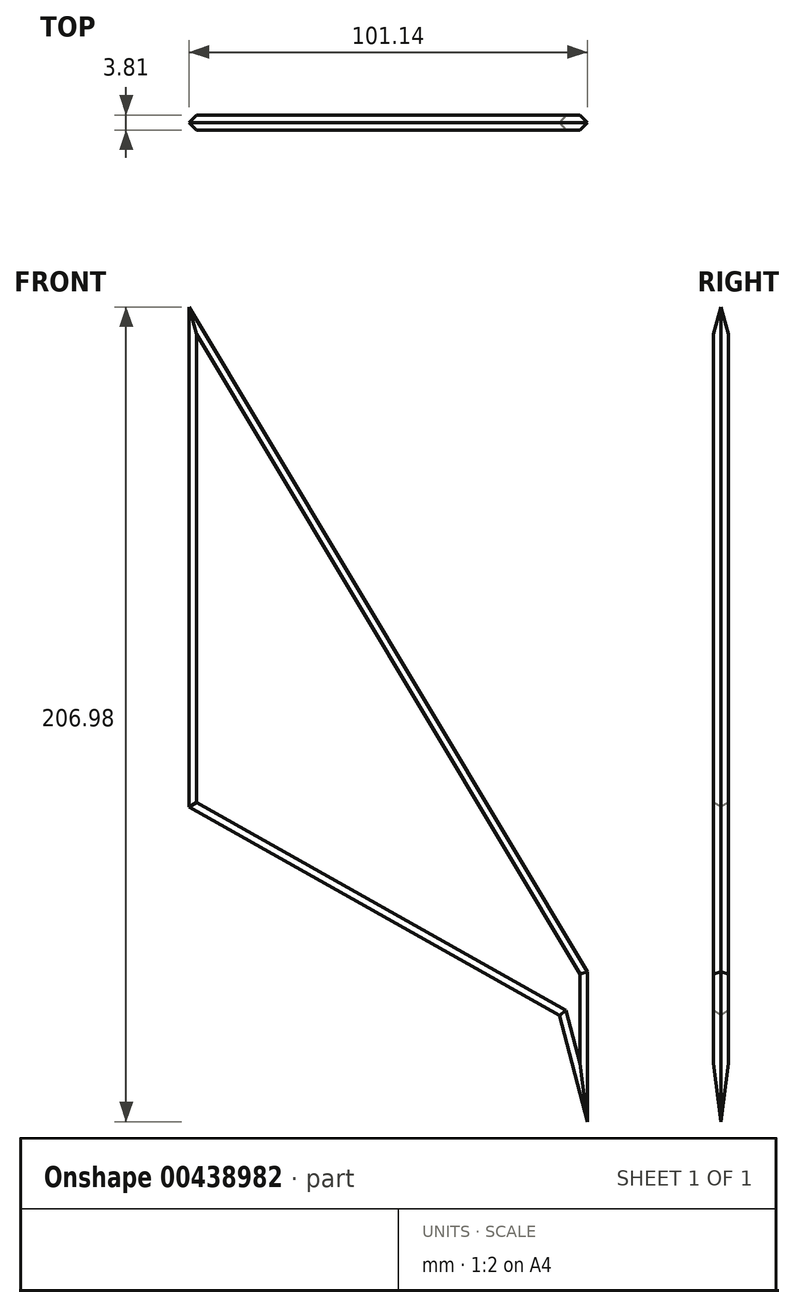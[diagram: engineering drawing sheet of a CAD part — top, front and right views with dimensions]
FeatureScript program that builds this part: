
annotation { "Feature Type Name" : "Feature", "Feature Type Description" : "" }
export const myFeature = defineFeature(function(context is Context, id is Id, definition is map)
    precondition{}
    {
        {
            var Q0;
            Q0=qCreatedBy(makeId("Front.planeOp"),FACE);
            var sketch = newSketch(context, id + "F0", { "sketchPlane" : qUnion([Q0])});
            skLineSegment(sketch, "E0", {"start": v(0, 92.94) * mm, "end": v(101.14, -75.94) * mm});
            skLineSegment(sketch, "E1", {"start": v(101.14, -75.94) * mm, "end": v(101.14, -114.04) * mm});
            skLineSegment(sketch, "E2", {"start": v(101.14, -114.04) * mm, "end": v(94.07, -87.01) * mm});
            skLineSegment(sketch, "E3", {"start": v(94.07, -87.01) * mm, "end": v(0, -34.06) * mm});
            skLineSegment(sketch, "E4", {"start": v(0, -34.06) * mm, "end": v(0, 92.94) * mm});
            skSolve(sketch);
        }
        {
            var Q0;
            Q0 = qSketchRegion(id + "F0", true);
            extrude(context, id + "F1", {"entities" : qUnion([Q0]), "depth" : 3.8 * mm});
        }
        {
            var Q0;
            Q0=makeQuery(id+"F1.opExtrude","CAP_FACE",FACE,{"disambiguationData":[OSD([sQuery(id+"F0.wireOp",EDGE,"E0"),sQuery(id+"F0.wireOp",EDGE,"E1"),sQuery(id+"F0.wireOp",EDGE,"E2"),sQuery(id+"F0.wireOp",EDGE,"E3"),sQuery(id+"F0.wireOp",EDGE,"E4")])],"isStart":false});
            var Q1;
            Q1=makeQuery(id+"F1.opExtrude","CAP_FACE",FACE,{"disambiguationData":[OSD([sQuery(id+"F0.wireOp",EDGE,"E0"),sQuery(id+"F0.wireOp",EDGE,"E1"),sQuery(id+"F0.wireOp",EDGE,"E2"),sQuery(id+"F0.wireOp",EDGE,"E3"),sQuery(id+"F0.wireOp",EDGE,"E4")])],"isStart":true});
            chamfer(context, id + "F2", {"entities" : qUnion([Q0, Q1]), "width" : 1.9 * mm, "tangentPropagation" : true});
        }
    });
